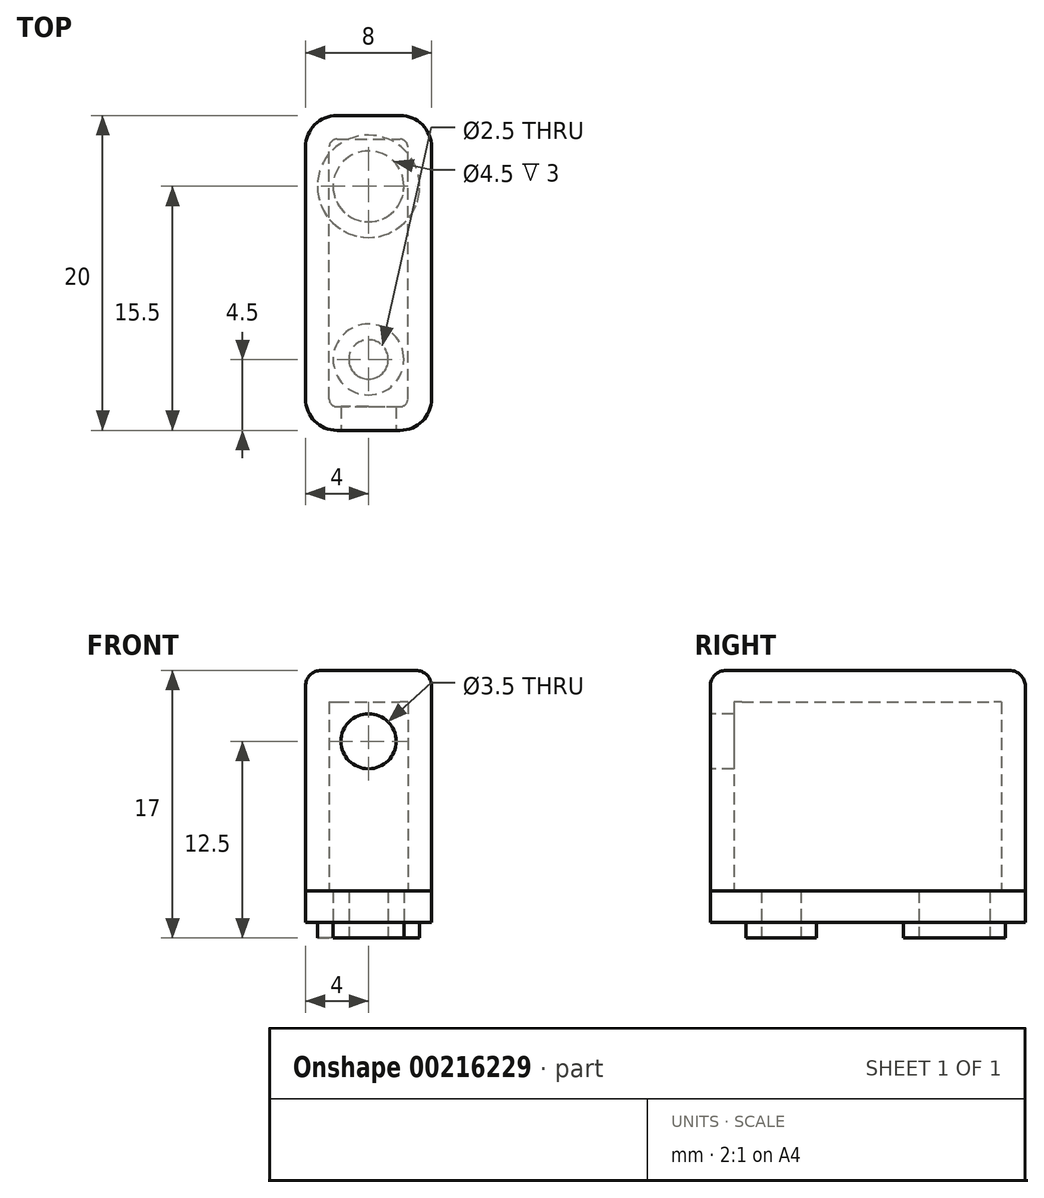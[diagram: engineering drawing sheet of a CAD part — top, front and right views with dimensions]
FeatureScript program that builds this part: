
annotation { "Feature Type Name" : "Feature", "Feature Type Description" : "" }
export const myFeature = defineFeature(function(context is Context, id is Id, definition is map)
    precondition{}
    {
        {
            var Q0;
            Q0=qCreatedBy(makeId("Top.planeOp"),FACE);
            var sketch = newSketch(context, id + "F0", { "sketchPlane" : qUnion([Q0])});
            skLineSegment(sketch, "E0.bottom", {"start": v(2, 0) * mm, "end": v(6, 0) * mm});
            skLineSegment(sketch, "E0.top", {"start": v(2, 20) * mm, "end": v(6, 20) * mm});
            skLineSegment(sketch, "E0.left", {"start": v(0, 2) * mm, "end": v(0, 18) * mm});
            skLineSegment(sketch, "E0.right", {"start": v(8, 2) * mm, "end": v(8, 18) * mm});
            skPoint(sketch, "E1.visualSharp", {"position": v(8, 20) * mm});
            skArc(sketch, "E1.filletArc", {"start": v(8, 18) * mm, "mid": v(7.41, 19.41) * mm, "end": v(6, 20) * mm});
            skPoint(sketch, "E2.visualSharp", {"position": v(0, 20) * mm});
            skArc(sketch, "E2.filletArc", {"start": v(2, 20) * mm, "mid": v(0.59, 19.41) * mm, "end": v(0, 18) * mm});
            skPoint(sketch, "E3.visualSharp", {"position": v(0, 0) * mm});
            skArc(sketch, "E3.filletArc", {"start": v(0, 2) * mm, "mid": v(0.59, 0.59) * mm, "end": v(2, 0) * mm});
            skPoint(sketch, "E4.visualSharp", {"position": v(8, 0) * mm});
            skArc(sketch, "E4.filletArc", {"start": v(6, 0) * mm, "mid": v(7.41, 0.59) * mm, "end": v(8, 2) * mm});
            skSolve(sketch);
        }
        {
            var Q0;
            Q0 = qSketchRegion(id + "F0", true);
            extrude(context, id + "F1", {"entities" : qUnion([Q0]), "depth" : 2 * mm});
        }
        {
            var Q0;
            Q0=makeQuery(id+"F1.opExtrude","CAP_FACE",FACE,{"disambiguationData":[OSD([sQuery(id+"F0.wireOp",EDGE,"E0.bottom"),sQuery(id+"F0.wireOp",EDGE,"E0.top"),sQuery(id+"F0.wireOp",EDGE,"E0.left"),sQuery(id+"F0.wireOp",EDGE,"E0.right")])],"isStart":true});
            var sketch = newSketch(context, id + "F2", { "sketchPlane" : qUnion([Q0])});
            skLineSegment(sketch, "E5", {"start": v(4, -20) * mm, "end": v(4, 0) * mm, "construction": true});
            skCircle(sketch, "E6", {"center": v(4, -15.5) * mm, "radius": 2.25 * mm});
            skCircle(sketch, "E7", {"center": v(4, -4.5) * mm, "radius": 1.25 * mm});
            skSolve(sketch);
        }
        {
            var Q0;
            Q0 = qSketchRegion(id + "F2", true);
            extrude(context, id + "F3", {"entities" : qUnion([Q0]), "operationType" : NewBodyOperationType.REMOVE, "endBound" : BoundingType.THROUGH_ALL, "oppositeDirection" : true, "depth" : 25 * mm});
        }
        {
            var Q0;
            Q0=makeQuery(id+"F1.opExtrude","CAP_FACE",FACE,{"disambiguationData":[OSD([sQuery(id+"F0.wireOp",EDGE,"E0.bottom"),sQuery(id+"F0.wireOp",EDGE,"E0.top"),sQuery(id+"F0.wireOp",EDGE,"E0.left"),sQuery(id+"F0.wireOp",EDGE,"E0.right")])],"isStart":true});
            var sketch = newSketch(context, id + "F4", { "sketchPlane" : qUnion([Q0])});
            skCircle(sketch, "E8", {"center": v(4, -4.5) * mm, "radius": 2.25 * mm});
            skCircle(sketch, "E9", {"center": v(4, -4.5) * mm, "radius": 1.25 * mm});
            skCircle(sketch, "E10", {"center": v(4, -15.5) * mm, "radius": 3.25 * mm});
            skCircle(sketch, "E11", {"center": v(4, -15.5) * mm, "radius": 2.25 * mm});
            skSolve(sketch);
        }
        {
            var Q0;
            Q0 = qSketchRegion(id + "F4", true);
            extrude(context, id + "F5", {"entities" : qUnion([Q0]), "operationType" : NewBodyOperationType.ADD, "depth" : 1 * mm});
        }
        {
            var Q0;
            Q0=makeQuery(id+"F1.opExtrude","CAP_FACE",FACE,{"disambiguationData":[OSD([sQuery(id+"F0.wireOp",EDGE,"E0.bottom"),sQuery(id+"F0.wireOp",EDGE,"E0.top"),sQuery(id+"F0.wireOp",EDGE,"E0.left"),sQuery(id+"F0.wireOp",EDGE,"E0.right"),sQuery(id+"F0.wireOp",EDGE,"E1.filletArc"),sQuery(id+"F0.wireOp",EDGE,"E2.filletArc"),sQuery(id+"F0.wireOp",EDGE,"E3.filletArc"),sQuery(id+"F0.wireOp",EDGE,"E4.filletArc")])],"isStart":false});
            var sketch = newSketch(context, id + "F6", { "sketchPlane" : qUnion([Q0])});
            skArc(sketch, "E12.0", {"start": v(1.5, 2) * mm, "mid": v(1.65, 1.65) * mm, "end": v(2, 1.5) * mm});
            skLineSegment(sketch, "E12.1", {"start": v(1.5, 2) * mm, "end": v(1.5, 18) * mm});
            skLineSegment(sketch, "E12.2", {"start": v(2, 1.5) * mm, "end": v(6, 1.5) * mm});
            skArc(sketch, "E12.3", {"start": v(2, 18.5) * mm, "mid": v(1.65, 18.35) * mm, "end": v(1.5, 18) * mm});
            skArc(sketch, "E12.4", {"start": v(6, 1.5) * mm, "mid": v(6.35, 1.65) * mm, "end": v(6.5, 2) * mm});
            skLineSegment(sketch, "E12.5", {"start": v(6.5, 2) * mm, "end": v(6.5, 18) * mm});
            skArc(sketch, "E12.6", {"start": v(6.5, 18) * mm, "mid": v(6.35, 18.35) * mm, "end": v(6, 18.5) * mm});
            skLineSegment(sketch, "E12.7", {"start": v(2, 18.5) * mm, "end": v(6, 18.5) * mm});
            skLineSegment(sketch, "E13.0", {"start": v(2, 0) * mm, "end": v(6, 0) * mm});
            skArc(sketch, "E13.1", {"start": v(0, 2) * mm, "mid": v(0.59, 0.59) * mm, "end": v(2, 0) * mm});
            skArc(sketch, "E13.2", {"start": v(6, 0) * mm, "mid": v(7.41, 0.59) * mm, "end": v(8, 2) * mm});
            skLineSegment(sketch, "E13.3", {"start": v(0, 2) * mm, "end": v(0, 18) * mm});
            skLineSegment(sketch, "E13.4", {"start": v(8, 2) * mm, "end": v(8, 18) * mm});
            skArc(sketch, "E13.5", {"start": v(8, 18) * mm, "mid": v(7.41, 19.41) * mm, "end": v(6, 20) * mm});
            skLineSegment(sketch, "E13.6", {"start": v(2, 20) * mm, "end": v(6, 20) * mm});
            skArc(sketch, "E13.7", {"start": v(2, 20) * mm, "mid": v(0.59, 19.41) * mm, "end": v(0, 18) * mm});
            skSolve(sketch);
        }
        {
            var Q0;
            Q0 = qSketchRegion(id + "F6", true);
            extrude(context, id + "F7", {"entities" : qUnion([Q0]), "depth" : 12 * mm});
        }
        {
            var Q0;
            Q0=makeQuery(id+"F7.opExtrude","SWEPT_FACE",FACE,{"disambiguationData":[OSD([sQuery(id+"F6.wireOp",EDGE,"E13.0")])]});
            var sketch = newSketch(context, id + "F8", { "sketchPlane" : qUnion([Q0])});
            skLineSegment(sketch, "E14", {"start": v(4, 14) * mm, "end": v(4, 2) * mm, "construction": true});
            skCircle(sketch, "E15", {"center": v(4, 11.5) * mm, "radius": 1.75 * mm});
            skSolve(sketch);
        }
        {
            var Q0;
            Q0 = qSketchRegion(id + "F8", true);
            extrude(context, id + "F9", {"entities" : qUnion([Q0]), "operationType" : NewBodyOperationType.REMOVE, "oppositeDirection" : true, "depth" : 4 * mm});
        }
        {
            var Q0;
            Q0=makeQuery(id+"F7.opExtrude","CAP_FACE",FACE,{"disambiguationData":[OSD([sQuery(id+"F6.wireOp",EDGE,"E12.0"),sQuery(id+"F6.wireOp",EDGE,"E12.1"),sQuery(id+"F6.wireOp",EDGE,"E12.2"),sQuery(id+"F6.wireOp",EDGE,"E12.3"),sQuery(id+"F6.wireOp",EDGE,"E12.4"),sQuery(id+"F6.wireOp",EDGE,"E12.5"),sQuery(id+"F6.wireOp",EDGE,"E12.6"),sQuery(id+"F6.wireOp",EDGE,"E12.7"),sQuery(id+"F6.wireOp",EDGE,"E13.0"),sQuery(id+"F6.wireOp",EDGE,"E13.1"),sQuery(id+"F6.wireOp",EDGE,"E13.2"),sQuery(id+"F6.wireOp",EDGE,"E13.3"),sQuery(id+"F6.wireOp",EDGE,"E13.4"),sQuery(id+"F6.wireOp",EDGE,"E13.5"),sQuery(id+"F6.wireOp",EDGE,"E13.6"),sQuery(id+"F6.wireOp",EDGE,"E13.7")])],"isStart":false});
            var sketch = newSketch(context, id + "F10", { "sketchPlane" : qUnion([Q0])});
            skArc(sketch, "E16.0", {"start": v(2, 20) * mm, "mid": v(0.59, 19.41) * mm, "end": v(0, 18) * mm});
            skLineSegment(sketch, "E16.1", {"start": v(0, 2) * mm, "end": v(0, 18) * mm});
            skLineSegment(sketch, "E16.2", {"start": v(2, 20) * mm, "end": v(6, 20) * mm});
            skArc(sketch, "E16.3", {"start": v(0, 2) * mm, "mid": v(0.59, 0.59) * mm, "end": v(2, 0) * mm});
            skArc(sketch, "E16.4", {"start": v(8, 18) * mm, "mid": v(7.41, 19.41) * mm, "end": v(6, 20) * mm});
            skLineSegment(sketch, "E16.5", {"start": v(8, 2) * mm, "end": v(8, 18) * mm});
            skArc(sketch, "E16.6", {"start": v(6, 0) * mm, "mid": v(7.41, 0.59) * mm, "end": v(8, 2) * mm});
            skLineSegment(sketch, "E16.7", {"start": v(2, 0) * mm, "end": v(6, 0) * mm});
            skSolve(sketch);
        }
        {
            var Q0;
            Q0 = qSketchRegion(id + "F10", true);
            extrude(context, id + "F11", {"entities" : qUnion([Q0]), "operationType" : NewBodyOperationType.ADD, "depth" : 2 * mm});
        }
        {
            var Q0;
            Q0=makeQuery(id+"F11.opExtrude","CAP_EDGE",EDGE,{"disambiguationData":[OSD([sQuery(id+"F10.wireOp",EDGE,"E16.5")])],"isStart":false});
            fillet(context, id + "F12", {"entities" : qUnion([Q0]), "radius" : 1 * mm, "tangentPropagation" : true, "allowEdgeOverflow" : false});
        }
    });
